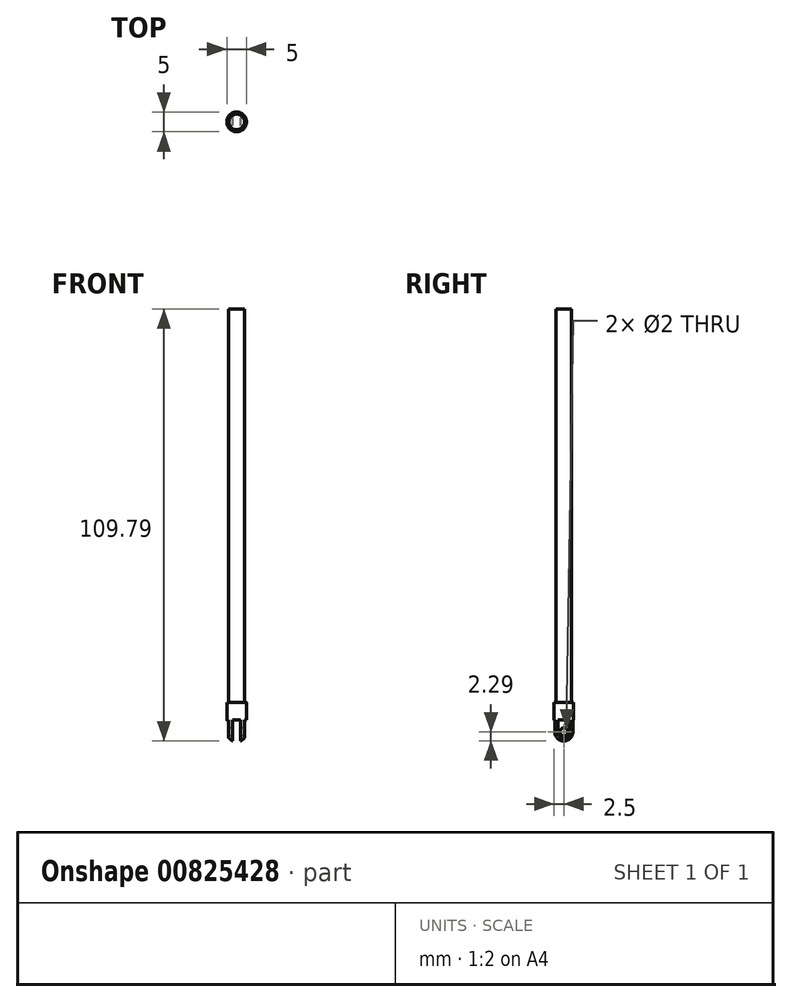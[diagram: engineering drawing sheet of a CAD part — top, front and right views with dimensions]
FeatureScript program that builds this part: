
annotation { "Feature Type Name" : "Feature", "Feature Type Description" : "" }
export const myFeature = defineFeature(function(context is Context, id is Id, definition is map)
    precondition{}
    {
        {
            var Q0;
            Q0=qCreatedBy(makeId("Top.planeOp"),FACE);
            var sketch = newSketch(context, id + "F0", { "sketchPlane" : qUnion([Q0])});
            skCircle(sketch, "E0", {"center": v(0, 0) * mm, "radius": 2 * mm});
            skSolve(sketch);
        }
        {
            var Q0;
            Q0=makeQuery(id+"F0.imprint","IMPRINT",FACE,{"disambiguationData":[TD([[makeQuery(id+"F0.imprint","IMPRINT",EDGE,{"derivedFrom":sQuery(id+"F0.wireOp",EDGE,"E0")}),1.0]])]});
            var Q1;
            Q1=sQuery(id+"F0.wireOp",EDGE,"E0");
            extrude(context, id + "F1", {"entities" : qUnion([Q0]), "surfaceEntities" : qUnion([Q1]), "depth" : 100 * mm, "offsetDistance" : 25 * mm});
        }
        {
            var Q0;
            Q0=makeQuery(id+"F1.opExtrude","CAP_FACE",FACE,{"disambiguationData":[OSD([sQuery(id+"F0.wireOp",EDGE,"E0")])],"isStart":true});
            var sketch = newSketch(context, id + "F2", { "sketchPlane" : qUnion([Q0])});
            skCircle(sketch, "E1", {"center": v(0, 0) * mm, "radius": 2.5 * mm});
            skSolve(sketch);
        }
        {
            var Q0;
            Q0 = qSketchRegion(id + "F2", true);
            extrude(context, id + "F3", {"entities" : qUnion([Q0]), "operationType" : NewBodyOperationType.ADD, "depth" : 10 * mm, "offsetDistance" : 25 * mm});
        }
        {
            var Q0;
            Q0=makeQuery(id+"F3.opExtrude","CAP_EDGE",EDGE,{"disambiguationData":[OSD([sQuery(id+"F2.wireOp",EDGE,"E1")])],"isStart":false});
            fillet(context, id + "F4", {"entities" : qUnion([Q0]), "radius" : 2.5 * mm, "tangentPropagation" : true, "allowEdgeOverflow" : false});
        }
        {
            var Q0;
            Q0=qCreatedBy(makeId("Front.planeOp"),FACE);
            var sketch = newSketch(context, id + "F5", { "sketchPlane" : qUnion([Q0])});
            skLineSegment(sketch, "E2", {"start": v(0, 0) * mm, "end": v(1, 0) * mm, "construction": true});
            skLineSegment(sketch, "E3", {"start": v(1, -4.5) * mm, "end": v(1, -10.38) * mm, "construction": true});
            skLineSegment(sketch, "E4", {"start": v(-1, -4.5) * mm, "end": v(-1, -10.38) * mm, "construction": true});
            skLineSegment(sketch, "E5", {"start": v(-2, -4.5) * mm, "end": v(-2, -10.38) * mm});
            skLineSegment(sketch, "E6", {"start": v(-1, -4.5) * mm, "end": v(-1, -10.38) * mm});
            skLineSegment(sketch, "E7", {"start": v(-2.72, -4.5) * mm, "end": v(-2.72, -10.38) * mm});
            skLineSegment(sketch, "E8", {"start": v(-2.72, -10.38) * mm, "end": v(-2, -10.38) * mm});
            skLineSegment(sketch, "E9", {"start": v(-1, -10.38) * mm, "end": v(1, -10.38) * mm});
            skLineSegment(sketch, "E10", {"start": v(1, 0) * mm, "end": v(-1, 0) * mm});
            skLineSegment(sketch, "E11", {"start": v(1, -4.5) * mm, "end": v(1, -10.38) * mm});
            skLineSegment(sketch, "E12", {"start": v(2, -4.5) * mm, "end": v(2, -10.38) * mm});
            skLineSegment(sketch, "E13", {"start": v(2, -10.38) * mm, "end": v(2.96, -10.38) * mm});
            skLineSegment(sketch, "E14", {"start": v(2.96, -10.38) * mm, "end": v(2.96, -4.5) * mm});
            skLineSegment(sketch, "E15", {"start": v(-2.72, -4.5) * mm, "end": v(-2, -4.5) * mm});
            skPoint(sketch, "E16.orphan", {"position": v(-2, 0) * mm});
            skPoint(sketch, "E17.start.orphan", {"position": v(2.96, 0) * mm});
            skLineSegment(sketch, "E18.trimOffspring", {"start": v(-1, -4.5) * mm, "end": v(1, -4.5) * mm});
            skLineSegment(sketch, "E19.trimOffspring", {"start": v(2, -4.5) * mm, "end": v(2.96, -4.5) * mm});
            skSolve(sketch);
        }
        {
            var Q0;
            Q0 = qSketchRegion(id + "F5", true);
            extrude(context, id + "F6", {"entities" : qUnion([Q0]), "operationType" : NewBodyOperationType.REMOVE, "endBound" : BoundingType.SYMMETRIC, "oppositeDirection" : true, "depth" : 6.16 * mm, "offsetDistance" : 25 * mm});
        }
        {
            var Q0;
            Q0=makeQuery(id+"F6.boolean.opBoolean","COPY",FACE,{"derivedFrom":makeQuery(id+"F6.opExtrude","SWEPT_FACE",FACE,{"disambiguationData":[OSD([sQuery(id+"F5.wireOp",EDGE,"E5")])]})});
            var sketch = newSketch(context, id + "F7", { "sketchPlane" : qUnion([Q0])});
            skCircle(sketch, "E20", {"center": v(0, -7.5) * mm, "radius": 1 * mm});
            skSolve(sketch);
        }
        {
            var Q0;
            Q0=makeQuery(id+"F7.imprint","IMPRINT",FACE,{"disambiguationData":[TD([[makeQuery(id+"F7.imprint","IMPRINT",EDGE,{"derivedFrom":sQuery(id+"F7.wireOp",EDGE,"E20")}),1.0]])]});
            var Q1;
            Q1=sQuery(id+"F7.wireOp",EDGE,"E20");
            extrude(context, id + "F8", {"entities" : qUnion([Q0]), "operationType" : NewBodyOperationType.REMOVE, "surfaceEntities" : qUnion([Q1]), "endBound" : BoundingType.THROUGH_ALL, "oppositeDirection" : true, "depth" : 25 * mm, "offsetDistance" : 25 * mm});
        }
    });
